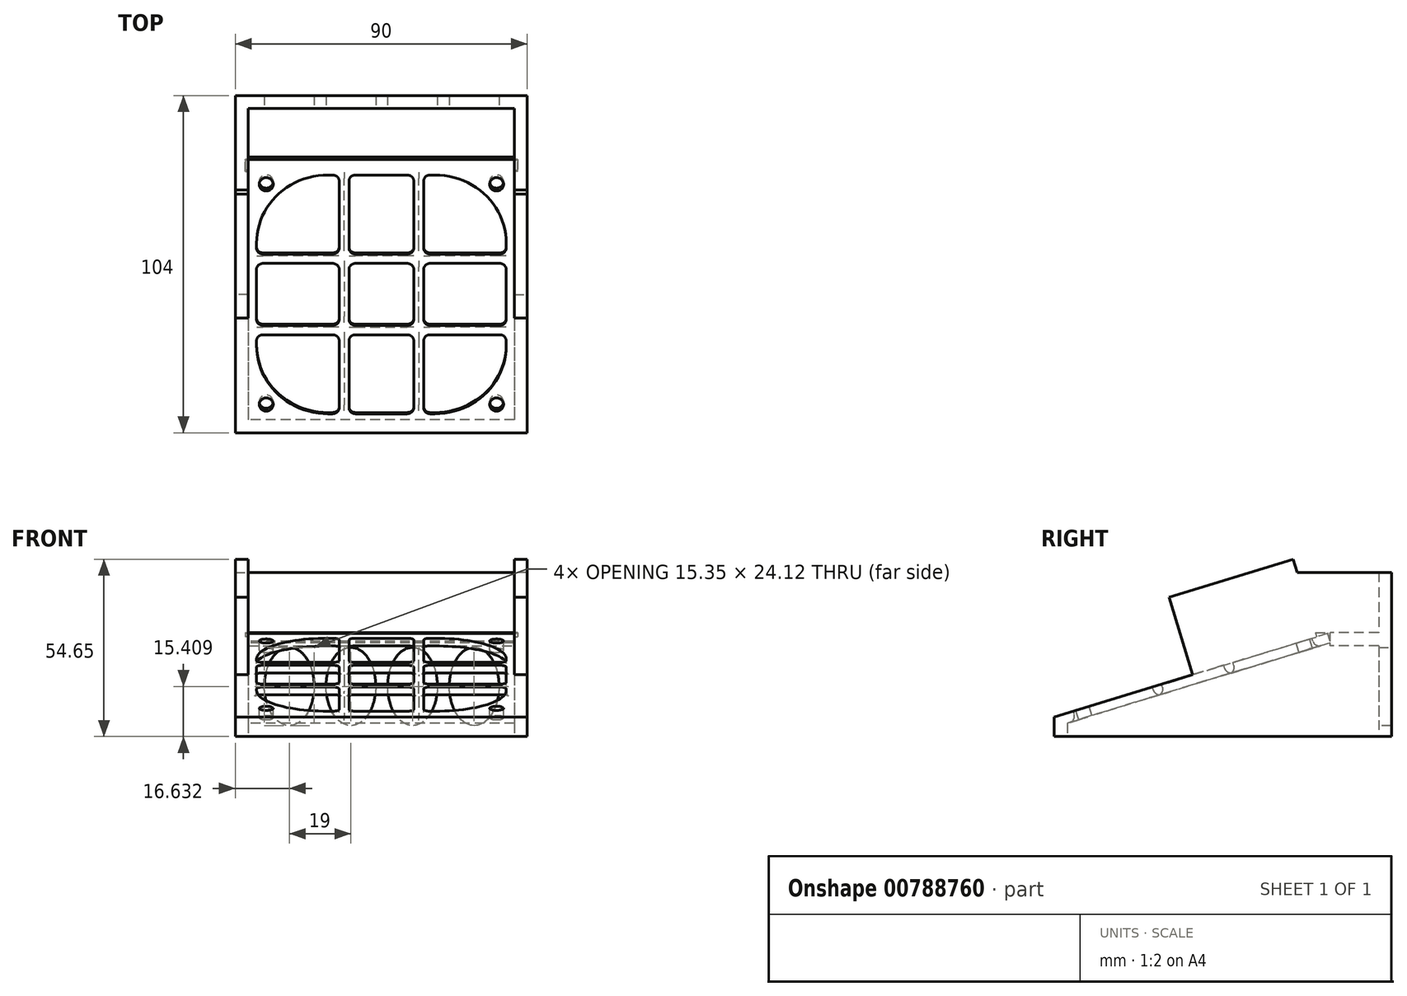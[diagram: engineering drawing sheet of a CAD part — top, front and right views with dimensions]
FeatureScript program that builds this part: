
annotation { "Feature Type Name" : "Feature", "Feature Type Description" : "" }
export const myFeature = defineFeature(function(context is Context, id is Id, definition is map)
    precondition{}
    {
        {
            var Q0;
            Q0=qCreatedBy(makeId("Top.planeOp"),FACE);
            var sketch = newSketch(context, id + "F0", { "sketchPlane" : qUnion([Q0])});
            skLineSegment(sketch, "E0.bottom", {"start": v(44.97, 44.9) * mm, "end": v(-45.03, 44.9) * mm, "construction": true});
            skLineSegment(sketch, "E0.top", {"start": v(44.97, -41.1) * mm, "end": v(-45.03, -41.1) * mm});
            skLineSegment(sketch, "E0.left", {"start": v(44.97, 44.9) * mm, "end": v(44.97, -41.1) * mm});
            skLineSegment(sketch, "E0.right", {"start": v(-45.03, 44.9) * mm, "end": v(-45.03, -41.1) * mm});
            skPoint(sketch, "E0.middle", {"position": v(0, 0) * mm});
            skLineSegment(sketch, "E1.0", {"start": v(40.97, 40.9) * mm, "end": v(-41.03, 40.9) * mm});
            skLineSegment(sketch, "E1.1", {"start": v(40.97, 40.9) * mm, "end": v(40.97, -37.1) * mm});
            skLineSegment(sketch, "E1.2", {"start": v(40.97, -37.1) * mm, "end": v(-41.03, -37.1) * mm});
            skLineSegment(sketch, "E1.3", {"start": v(-41.03, 40.9) * mm, "end": v(-41.03, -37.1) * mm});
            skLineSegment(sketch, "E2", {"start": v(-45.03, 44.9) * mm, "end": v(-45.03, 62.9) * mm});
            skLineSegment(sketch, "E3", {"start": v(-45.03, 62.9) * mm, "end": v(44.97, 62.9) * mm});
            skLineSegment(sketch, "E4", {"start": v(44.97, 62.9) * mm, "end": v(44.97, 44.9) * mm});
            skLineSegment(sketch, "E5", {"start": v(-41.03, 40.9) * mm, "end": v(-41.03, 58.9) * mm});
            skLineSegment(sketch, "E6", {"start": v(-41.03, 58.9) * mm, "end": v(40.97, 58.9) * mm});
            skLineSegment(sketch, "E7", {"start": v(40.97, 58.9) * mm, "end": v(40.97, 40.9) * mm});
            skSolve(sketch);
        }
        {
            var Q0;
            Q0=makeQuery(id+"F0.imprint","IMPRINT",FACE,{"disambiguationData":[TD([[makeQuery(id+"F0.imprint","IMPRINT",EDGE,{"derivedFrom":sQuery(id+"F0.wireOp",EDGE,"E0.top")}),-1.0]])]});
            var Q1;
            {var subQ0=sQuery(id+"F0.wireOp",EDGE,"E2");Q1=makeQuery(id+"F0.imprint","IMPRINT",FACE,{"disambiguationData":[TD([[makeQuery(id+"F0.imprint","IMPRINT",EDGE,{"derivedFrom":subQ0}),-1.0]])]});}
            extrude(context, id + "F1", {"entities" : qUnion([Q0, Q1]), "depth" : 32 * mm, "offsetDistance" : 25 * mm});
        }
        {
            var Q0;
            Q0=makeQuery(id+"F1.opExtrude","CAP_EDGE",EDGE,{"disambiguationData":[OSD([sQuery(id+"F0.wireOp",EDGE,"E0.top")])],"isStart":false});
            chamfer(context, id + "F2", {"entities" : qUnion([Q0]), "chamferType" : ChamferType.OFFSET_ANGLE, "width" : 26 * mm, "oppositeDirection" : false, "angle" : 73 * degree, "tangentPropagation" : true});
        }
        {
            var Q0;
            Q0=makeQuery(id+"F2.opChamfer","BLEND_FACE",FACE,{"disambiguationData":[OSD([sQuery(id+"F0.wireOp",EDGE,"E0.top")])]});
            var sketch = newSketch(context, id + "F3", { "sketchPlane" : qUnion([Q0])});
            skLineSegment(sketch, "E8.bottom", {"start": v(42, 50.58) * mm, "end": v(-42, 50.58) * mm});
            skLineSegment(sketch, "E8.top", {"start": v(42, -36.42) * mm, "end": v(-42, -36.42) * mm, "construction": true});
            skLineSegment(sketch, "E8.left", {"start": v(42, 50.58) * mm, "end": v(42, -36.42) * mm});
            skLineSegment(sketch, "E8.right", {"start": v(-42, 50.58) * mm, "end": v(-42, -36.42) * mm});
            skPoint(sketch, "E8.middle", {"position": v(0, 7.08) * mm});
            skLineSegment(sketch, "E9.bottom", {"start": v(16.5, 45.58) * mm, "end": v(13, 45.58) * mm});
            skLineSegment(sketch, "E9.top", {"start": v(16.5, -31.42) * mm, "end": v(13, -31.42) * mm});
            skLineSegment(sketch, "E9.left", {"start": v(38.5, 23.58) * mm, "end": v(38.5, 20.08) * mm});
            skLineSegment(sketch, "E9.right", {"start": v(-38.5, 23.58) * mm, "end": v(-38.5, 20.08) * mm});
            skArc(sketch, "E10.filletArc", {"start": v(38.5, 23.58) * mm, "mid": v(32.06, 39.14) * mm, "end": v(16.5, 45.58) * mm});
            skArc(sketch, "E11.filletArc", {"start": v(-16.5, 45.58) * mm, "mid": v(-32.06, 39.14) * mm, "end": v(-38.5, 23.58) * mm});
            skArc(sketch, "E12.filletArc", {"start": v(-38.5, -9.42) * mm, "mid": v(-32.06, -24.98) * mm, "end": v(-16.5, -31.42) * mm});
            skArc(sketch, "E13.filletArc", {"start": v(16.5, -31.42) * mm, "mid": v(32.06, -24.98) * mm, "end": v(38.5, -9.42) * mm});
            skLineSegment(sketch, "E14", {"start": v(16.5, -31.42) * mm, "end": v(16.5, 45.58) * mm, "construction": true});
            skLineSegment(sketch, "E15.bottom", {"start": v(35.5, 42.58) * mm, "end": v(-35.5, 42.58) * mm, "construction": true});
            skLineSegment(sketch, "E15.top", {"start": v(35.5, -28.42) * mm, "end": v(-35.5, -28.42) * mm, "construction": true});
            skLineSegment(sketch, "E15.left", {"start": v(35.5, 42.58) * mm, "end": v(35.5, -28.42) * mm, "construction": true});
            skLineSegment(sketch, "E15.right", {"start": v(-35.5, 42.58) * mm, "end": v(-35.5, -28.42) * mm, "construction": true});
            skCircle(sketch, "E16", {"center": v(-35.5, 42.58) * mm, "radius": 2.15 * mm});
            skCircle(sketch, "E17.MirrorC", {"center": v(35.5, 42.58) * mm, "radius": 2.15 * mm});
            skCircle(sketch, "E18.MirrorC", {"center": v(35.5, -28.42) * mm, "radius": 2.15 * mm});
            skCircle(sketch, "E19.MirrorC", {"center": v(-35.5, -28.42) * mm, "radius": 2.15 * mm});
            skLineSegment(sketch, "E20.bottom", {"start": v(40, 47.08) * mm, "end": v(-40, 47.08) * mm});
            skLineSegment(sketch, "E20.top", {"start": v(40, -32.92) * mm, "end": v(-40, -32.92) * mm});
            skLineSegment(sketch, "E20.left", {"start": v(40, 47.08) * mm, "end": v(40, -32.92) * mm});
            skLineSegment(sketch, "E20.right", {"start": v(-40, 47.08) * mm, "end": v(-40, -32.92) * mm});
            skLineSegment(sketch, "E21", {"start": v(-42, 7.08) * mm, "end": v(42, 7.08) * mm, "construction": true});
            skLineSegment(sketch, "E22", {"start": v(0, 50.58) * mm, "end": v(0, -36.42) * mm, "construction": true});
            skLineSegment(sketch, "E23", {"start": v(13, -31.42) * mm, "end": v(13, -5.92) * mm});
            skLineSegment(sketch, "E24", {"start": v(10, -31.42) * mm, "end": v(10, -5.92) * mm});
            skLineSegment(sketch, "E25.MirrorCS", {"start": v(-10, -31.42) * mm, "end": v(-10, -5.92) * mm});
            skLineSegment(sketch, "E26.MirrorCS", {"start": v(-13, -31.42) * mm, "end": v(-13, -5.92) * mm});
            skLineSegment(sketch, "E27.trimOffspring", {"start": v(-13, -31.42) * mm, "end": v(-16.5, -31.42) * mm});
            skLineSegment(sketch, "E28.trimOffspring", {"start": v(-13, 45.58) * mm, "end": v(-16.5, 45.58) * mm});
            skLineSegment(sketch, "E29.trimOffspring", {"start": v(10, 45.58) * mm, "end": v(-10, 45.58) * mm});
            skLineSegment(sketch, "E30.trimOffspring", {"start": v(10, -31.42) * mm, "end": v(-10, -31.42) * mm});
            skLineSegment(sketch, "E31", {"start": v(-38.5, -5.92) * mm, "end": v(-13, -5.92) * mm});
            skLineSegment(sketch, "E32", {"start": v(38.5, -2.92) * mm, "end": v(13, -2.92) * mm});
            skLineSegment(sketch, "E33", {"start": v(10, 45.58) * mm, "end": v(13, 45.58) * mm, "construction": true});
            skLineSegment(sketch, "E34.trimOffspring", {"start": v(38.5, -5.92) * mm, "end": v(38.5, -9.42) * mm});
            skLineSegment(sketch, "E35", {"start": v(38.5, -5.92) * mm, "end": v(38.5, -2.92) * mm, "construction": true});
            skPoint(sketch, "E36", {"position": v(35.5, 7.08) * mm});
            skPoint(sketch, "E37", {"position": v(0, 45.58) * mm});
            skLineSegment(sketch, "E38.MirrorCS", {"start": v(38.5, 17.08) * mm, "end": v(13, 17.08) * mm});
            skLineSegment(sketch, "E39.MirrorCS", {"start": v(-38.5, 20.08) * mm, "end": v(-13, 20.08) * mm});
            skLineSegment(sketch, "E40.trimOffspring", {"start": v(38.5, 17.08) * mm, "end": v(38.5, -2.92) * mm});
            skLineSegment(sketch, "E41.trimOffspring", {"start": v(-38.5, 17.08) * mm, "end": v(-38.5, -2.92) * mm});
            skLineSegment(sketch, "E42.trimOffspring", {"start": v(-38.5, -5.92) * mm, "end": v(-38.5, -9.42) * mm});
            skLineSegment(sketch, "E43.trimOffspring", {"start": v(-10, -2.92) * mm, "end": v(-10, 17.08) * mm});
            skLineSegment(sketch, "E44.trimOffspring", {"start": v(-13, -2.92) * mm, "end": v(-38.5, -2.92) * mm});
            skLineSegment(sketch, "E45.trimOffspring", {"start": v(-13, -2.92) * mm, "end": v(-13, 17.08) * mm});
            skLineSegment(sketch, "E46.trimOffspring", {"start": v(-10, -5.92) * mm, "end": v(10, -5.92) * mm});
            skLineSegment(sketch, "E47.trimOffspring", {"start": v(-13, 17.08) * mm, "end": v(-38.5, 17.08) * mm});
            skLineSegment(sketch, "E48.trimOffspring", {"start": v(-13, 20.08) * mm, "end": v(-13, 45.58) * mm});
            skLineSegment(sketch, "E49.trimOffspring", {"start": v(-10, 20.08) * mm, "end": v(10, 20.08) * mm});
            skLineSegment(sketch, "E50.trimOffspring", {"start": v(-10, 20.08) * mm, "end": v(-10, 45.58) * mm});
            skLineSegment(sketch, "E51.trimOffspring", {"start": v(13, 20.08) * mm, "end": v(13, 45.58) * mm});
            skLineSegment(sketch, "E52.trimOffspring", {"start": v(10, 17.08) * mm, "end": v(-10, 17.08) * mm});
            skLineSegment(sketch, "E53.trimOffspring", {"start": v(10, 20.08) * mm, "end": v(10, 45.58) * mm});
            skLineSegment(sketch, "E54.trimOffspring", {"start": v(13, 20.08) * mm, "end": v(38.5, 20.08) * mm});
            skLineSegment(sketch, "E55.trimOffspring", {"start": v(13, -2.92) * mm, "end": v(13, 17.08) * mm});
            skLineSegment(sketch, "E56.trimOffspring", {"start": v(10, -2.92) * mm, "end": v(-10, -2.92) * mm});
            skLineSegment(sketch, "E57.trimOffspring", {"start": v(10, -2.92) * mm, "end": v(10, 17.08) * mm});
            skLineSegment(sketch, "E58.trimOffspring", {"start": v(13, -5.92) * mm, "end": v(38.5, -5.92) * mm});
            skLineSegment(sketch, "E59", {"start": v(-40, -32.92) * mm, "end": v(-42, -32.92) * mm});
            skLineSegment(sketch, "E60", {"start": v(40, -32.92) * mm, "end": v(42, -32.92) * mm});
            skLineSegment(sketch, "E61", {"start": v(-42, -34.56) * mm, "end": v(42, -34.56) * mm});
            skLineSegment(sketch, "E62", {"start": v(-42, -36.42) * mm, "end": v(-42, -37.56) * mm, "construction": true});
            skLineSegment(sketch, "E63", {"start": v(-42, -37.56) * mm, "end": v(42, -37.56) * mm});
            skLineSegment(sketch, "E64", {"start": v(42, -37.56) * mm, "end": v(42, -36.42) * mm, "construction": true});
            skLineSegment(sketch, "E65", {"start": v(-42, -34.56) * mm, "end": v(-45.03, -34.56) * mm});
            skLineSegment(sketch, "E66", {"start": v(-45.03, -34.56) * mm, "end": v(-45.03, -37.56) * mm});
            skLineSegment(sketch, "E67", {"start": v(-45.03, -37.56) * mm, "end": v(-42, -37.56) * mm});
            skLineSegment(sketch, "E68", {"start": v(42, -34.56) * mm, "end": v(44.97, -34.56) * mm});
            skLineSegment(sketch, "E69", {"start": v(44.97, -34.56) * mm, "end": v(44.97, -37.56) * mm});
            skLineSegment(sketch, "E70", {"start": v(44.97, -37.56) * mm, "end": v(42, -37.56) * mm});
            skLineSegment(sketch, "E71", {"start": v(40, 47.08) * mm, "end": v(42, 47.08) * mm});
            skLineSegment(sketch, "E72", {"start": v(-40, 47.08) * mm, "end": v(-42, 47.08) * mm});
            skLineSegment(sketch, "E73", {"start": v(40.97, 47.08) * mm, "end": v(44.97, 47.08) * mm});
            skLineSegment(sketch, "E74", {"start": v(-41.03, 47.08) * mm, "end": v(-45.03, 47.08) * mm});
            skLineSegment(sketch, "E75", {"start": v(-41.03, 7.08) * mm, "end": v(-45.03, 7.08) * mm});
            skLineSegment(sketch, "E76", {"start": v(40.97, 7.08) * mm, "end": v(44.97, 7.08) * mm});
            skSolve(sketch);
        }
        {
            var Q0;
            Q0 = qSketchRegion(id + "F3", true);
            var Q1;
            {var subQ42=sQuery(id+"F3.wireOp",EDGE,"E9.top");Q1=makeQuery(id+"F3.imprint","IMPRINT",FACE,{"disambiguationData":[TD([[makeQuery(id+"F3.imprint","IMPRINT",EDGE,{"derivedFrom":subQ42}),1.0]])]});}
            var Q2;
            {var subQ0=sQuery(id+"F3.wireOp",EDGE,"E13.filletArc");var subQ1=makeQuery(id+"F1.opExtrude","CAP_EDGE",EDGE,{"disambiguationData":[OSD([sQuery(id+"F0.wireOp",EDGE,"E0.top")])],"isStart":false});var subQ2=makeQuery(id+"F2.opChamfer","BLEND_EDGE",EDGE,{"blendedFrom":[subQ1,makeQuery(id+"F1.opExtrude","SWEPT_FACE",FACE,{"disambiguationData":[OSD([sQuery(id+"F0.wireOp",EDGE,"E1.2")])]})],"blendedInto":[makeQuery(id+"F1.opExtrude","SWEPT_FACE",FACE,{"disambiguationData":[OSD([sQuery(id+"F0.wireOp",EDGE,"E1.2")])]})]});var subQ3=makeQuery(id+"F3.imprint","INTERSECT",VERTEX,{"derivedFrom":[subQ2,subQ0]});Q2=makeQuery(id+"F3.imprint","IMPRINT",FACE,{"disambiguationData":[TD([[makeQuery(id+"F3.imprint","IMPRINT",EDGE,{"disambiguationData":[TD([[subQ3,-1.0]])],"derivedFrom":subQ0}),-1.0]])]});}
            var Q3;
            {var subQ0=sQuery(id+"F3.wireOp",EDGE,"E12.filletArc");var subQ1=makeQuery(id+"F1.opExtrude","CAP_EDGE",EDGE,{"disambiguationData":[OSD([sQuery(id+"F0.wireOp",EDGE,"E0.top")])],"isStart":false});var subQ2=makeQuery(id+"F2.opChamfer","BLEND_EDGE",EDGE,{"blendedFrom":[subQ1,makeQuery(id+"F1.opExtrude","SWEPT_FACE",FACE,{"disambiguationData":[OSD([sQuery(id+"F0.wireOp",EDGE,"E1.3")])]})],"blendedInto":[makeQuery(id+"F1.opExtrude","SWEPT_FACE",FACE,{"disambiguationData":[OSD([sQuery(id+"F0.wireOp",EDGE,"E1.3")])]})]});var subQ3=makeQuery(id+"F3.imprint","INTERSECT",VERTEX,{"derivedFrom":[subQ2,subQ0]});Q3=makeQuery(id+"F3.imprint","IMPRINT",FACE,{"disambiguationData":[TD([[makeQuery(id+"F3.imprint","IMPRINT",EDGE,{"disambiguationData":[TD([[subQ3,-1.0]])],"derivedFrom":subQ0}),-1.0]])]});}
            var Q4;
            {var subQ11=sQuery(id+"F3.wireOp",EDGE,"E9.bottom");Q4=makeQuery(id+"F3.imprint","IMPRINT",FACE,{"disambiguationData":[TD([[makeQuery(id+"F3.imprint","IMPRINT",EDGE,{"derivedFrom":subQ11}),-1.0]])]});}
            extrude(context, id + "F4", {"entities" : qUnion([Q0, Q1, Q2, Q3, Q4]), "operationType" : NewBodyOperationType.ADD, "oppositeDirection" : true, "depth" : 3 * mm, "offsetDistance" : 25 * mm});
        }
        {
            var Q0;
            Q0=makeQuery(id+"F1.opExtrude","SWEPT_FACE",FACE,{"disambiguationData":[OSD([sQuery(id+"F0.wireOp",EDGE,"E3")])]});
            var sketch = newSketch(context, id + "F5", { "sketchPlane" : qUnion([Q0])});
            skEllipse(sketch, "E77", {"center": v(-28.6, 15.4) * mm, "majorRadius": 12.06 * mm, "minorRadius": 7.68 * mm, "majorAxis": v(0, 1)});
            skEllipse(sketch, "E78.1.0.0", {"center": v(-9.6, 15.4) * mm, "majorRadius": 12.06 * mm, "minorRadius": 7.68 * mm, "majorAxis": v(0, 1)});
            skEllipse(sketch, "E78.2.0.0", {"center": v(9.4, 15.4) * mm, "majorRadius": 12.06 * mm, "minorRadius": 7.68 * mm, "majorAxis": v(0, 1)});
            skEllipse(sketch, "E78.3.0.0", {"center": v(28.4, 15.4) * mm, "majorRadius": 12.06 * mm, "minorRadius": 7.68 * mm, "majorAxis": v(0, 1)});
            skLineSegment(sketch, "E78.direction1", {"start": v(-28.6, 15.4) * mm, "end": v(-9.6, 15.4) * mm, "construction": true});
            skSolve(sketch);
        }
        {
            var Q0;
            Q0 = qSketchRegion(id + "F5", true);
            extrude(context, id + "F6", {"entities" : qUnion([Q0]), "operationType" : NewBodyOperationType.REMOVE, "oppositeDirection" : true, "depth" : 5 * mm, "offsetDistance" : 25 * mm});
        }
        {
            var Q0;
            Q0=makeQuery(id+"F4.opExtrude","SWEPT_EDGE",EDGE,{"disambiguationData":[OSD([sQuery(id+"F3.wireOp",EDGE,"E45.trimOffspring"),sQuery(id+"F3.wireOp",EDGE,"E47.trimOffspring")])]});
            var Q1;
            Q1=makeQuery(id+"F4.opExtrude","SWEPT_EDGE",EDGE,{"disambiguationData":[OSD([sQuery(id+"F3.wireOp",EDGE,"E52.trimOffspring"),sQuery(id+"F3.wireOp",EDGE,"E57.trimOffspring")])]});
            var Q2;
            Q2=makeQuery(id+"F4.opExtrude","SWEPT_EDGE",EDGE,{"disambiguationData":[OSD([sQuery(id+"F3.wireOp",EDGE,"E24"),sQuery(id+"F3.wireOp",EDGE,"E46.trimOffspring")])]});
            var Q3;
            Q3=makeQuery(id+"F4.opExtrude","SWEPT_EDGE",EDGE,{"disambiguationData":[OSD([sQuery(id+"F3.wireOp",EDGE,"E26.MirrorCS"),sQuery(id+"F3.wireOp",EDGE,"E31")])]});
            var Q4;
            Q4=makeQuery(id+"F4.opExtrude","SWEPT_EDGE",EDGE,{"disambiguationData":[OSD([sQuery(id+"F3.wireOp",EDGE,"E25.MirrorCS"),sQuery(id+"F3.wireOp",EDGE,"E46.trimOffspring")])]});
            var Q5;
            Q5=makeQuery(id+"F4.opExtrude","SWEPT_EDGE",EDGE,{"disambiguationData":[OSD([sQuery(id+"F3.wireOp",EDGE,"E43.trimOffspring"),sQuery(id+"F3.wireOp",EDGE,"E52.trimOffspring")])]});
            var Q6;
            Q6=makeQuery(id+"F4.opExtrude","SWEPT_EDGE",EDGE,{"disambiguationData":[OSD([sQuery(id+"F3.wireOp",EDGE,"E41.trimOffspring"),sQuery(id+"F3.wireOp",EDGE,"E47.trimOffspring")])]});
            var Q7;
            Q7=makeQuery(id+"F4.opExtrude","SWEPT_EDGE",EDGE,{"disambiguationData":[OSD([sQuery(id+"F3.wireOp",EDGE,"E31"),sQuery(id+"F3.wireOp",EDGE,"E42.trimOffspring")])]});
            var Q8;
            Q8=makeQuery(id+"F4.opExtrude","SWEPT_EDGE",EDGE,{"disambiguationData":[OSD([sQuery(id+"F3.wireOp",EDGE,"E23"),sQuery(id+"F3.wireOp",EDGE,"E58.trimOffspring")])]});
            var Q9;
            Q9=makeQuery(id+"F4.opExtrude","SWEPT_EDGE",EDGE,{"disambiguationData":[OSD([sQuery(id+"F3.wireOp",EDGE,"E38.MirrorCS"),sQuery(id+"F3.wireOp",EDGE,"E55.trimOffspring")])]});
            var Q10;
            Q10=makeQuery(id+"F4.opExtrude","SWEPT_EDGE",EDGE,{"disambiguationData":[OSD([sQuery(id+"F3.wireOp",EDGE,"E9.bottom"),sQuery(id+"F3.wireOp",EDGE,"E51.trimOffspring")])]});
            var Q11;
            Q11=makeQuery(id+"F4.opExtrude","SWEPT_EDGE",EDGE,{"disambiguationData":[OSD([sQuery(id+"F3.wireOp",EDGE,"E29.trimOffspring"),sQuery(id+"F3.wireOp",EDGE,"E50.trimOffspring")])]});
            var Q12;
            Q12=makeQuery(id+"F4.opExtrude","SWEPT_EDGE",EDGE,{"disambiguationData":[OSD([sQuery(id+"F3.wireOp",EDGE,"E38.MirrorCS"),sQuery(id+"F3.wireOp",EDGE,"E40.trimOffspring")])]});
            var Q13;
            Q13=makeQuery(id+"F4.opExtrude","SWEPT_EDGE",EDGE,{"disambiguationData":[OSD([sQuery(id+"F3.wireOp",EDGE,"E34.trimOffspring"),sQuery(id+"F3.wireOp",EDGE,"E58.trimOffspring")])]});
            var Q14;
            Q14=makeQuery(id+"F4.opExtrude","SWEPT_EDGE",EDGE,{"disambiguationData":[OSD([sQuery(id+"F3.wireOp",EDGE,"E29.trimOffspring"),sQuery(id+"F3.wireOp",EDGE,"E53.trimOffspring")])]});
            var Q15;
            Q15=makeQuery(id+"F4.opExtrude","SWEPT_EDGE",EDGE,{"disambiguationData":[OSD([sQuery(id+"F3.wireOp",EDGE,"E28.trimOffspring"),sQuery(id+"F3.wireOp",EDGE,"E48.trimOffspring")])]});
            var Q16;
            Q16=makeQuery(id+"F4.opExtrude","SWEPT_EDGE",EDGE,{"disambiguationData":[OSD([sQuery(id+"F3.wireOp",EDGE,"E25.MirrorCS"),sQuery(id+"F3.wireOp",EDGE,"E30.trimOffspring")])]});
            var Q17;
            Q17=makeQuery(id+"F4.opExtrude","SWEPT_EDGE",EDGE,{"disambiguationData":[OSD([sQuery(id+"F3.wireOp",EDGE,"E9.top"),sQuery(id+"F3.wireOp",EDGE,"E23")])]});
            var Q18;
            Q18=makeQuery(id+"F4.opExtrude","SWEPT_EDGE",EDGE,{"disambiguationData":[OSD([sQuery(id+"F3.wireOp",EDGE,"E32"),sQuery(id+"F3.wireOp",EDGE,"E55.trimOffspring")])]});
            var Q19;
            Q19=makeQuery(id+"F4.opExtrude","SWEPT_EDGE",EDGE,{"disambiguationData":[OSD([sQuery(id+"F3.wireOp",EDGE,"E51.trimOffspring"),sQuery(id+"F3.wireOp",EDGE,"E54.trimOffspring")])]});
            var Q20;
            Q20=makeQuery(id+"F4.opExtrude","SWEPT_EDGE",EDGE,{"disambiguationData":[OSD([sQuery(id+"F3.wireOp",EDGE,"E49.trimOffspring"),sQuery(id+"F3.wireOp",EDGE,"E50.trimOffspring")])]});
            var Q21;
            Q21=makeQuery(id+"F4.opExtrude","SWEPT_EDGE",EDGE,{"disambiguationData":[OSD([sQuery(id+"F3.wireOp",EDGE,"E43.trimOffspring"),sQuery(id+"F3.wireOp",EDGE,"E56.trimOffspring")])]});
            var Q22;
            Q22=makeQuery(id+"F4.opExtrude","SWEPT_EDGE",EDGE,{"disambiguationData":[OSD([sQuery(id+"F3.wireOp",EDGE,"E41.trimOffspring"),sQuery(id+"F3.wireOp",EDGE,"E44.trimOffspring")])]});
            var Q23;
            Q23=makeQuery(id+"F4.opExtrude","SWEPT_EDGE",EDGE,{"disambiguationData":[OSD([sQuery(id+"F3.wireOp",EDGE,"E9.right"),sQuery(id+"F3.wireOp",EDGE,"E39.MirrorCS")])]});
            var Q24;
            Q24=makeQuery(id+"F4.opExtrude","SWEPT_EDGE",EDGE,{"disambiguationData":[OSD([sQuery(id+"F3.wireOp",EDGE,"E39.MirrorCS"),sQuery(id+"F3.wireOp",EDGE,"E48.trimOffspring")])]});
            var Q25;
            Q25=makeQuery(id+"F4.opExtrude","SWEPT_EDGE",EDGE,{"disambiguationData":[OSD([sQuery(id+"F3.wireOp",EDGE,"E24"),sQuery(id+"F3.wireOp",EDGE,"E30.trimOffspring")])]});
            var Q26;
            Q26=makeQuery(id+"F4.opExtrude","SWEPT_EDGE",EDGE,{"disambiguationData":[OSD([sQuery(id+"F3.wireOp",EDGE,"E26.MirrorCS"),sQuery(id+"F3.wireOp",EDGE,"E27.trimOffspring")])]});
            var Q27;
            Q27=makeQuery(id+"F4.opExtrude","SWEPT_EDGE",EDGE,{"disambiguationData":[OSD([sQuery(id+"F3.wireOp",EDGE,"E32"),sQuery(id+"F3.wireOp",EDGE,"E40.trimOffspring")])]});
            var Q28;
            Q28=makeQuery(id+"F4.opExtrude","SWEPT_EDGE",EDGE,{"disambiguationData":[OSD([sQuery(id+"F3.wireOp",EDGE,"E9.left"),sQuery(id+"F3.wireOp",EDGE,"E54.trimOffspring")])]});
            var Q29;
            Q29=makeQuery(id+"F4.opExtrude","SWEPT_EDGE",EDGE,{"disambiguationData":[OSD([sQuery(id+"F3.wireOp",EDGE,"E56.trimOffspring"),sQuery(id+"F3.wireOp",EDGE,"E57.trimOffspring")])]});
            var Q30;
            Q30=makeQuery(id+"F4.opExtrude","SWEPT_EDGE",EDGE,{"disambiguationData":[OSD([sQuery(id+"F3.wireOp",EDGE,"E49.trimOffspring"),sQuery(id+"F3.wireOp",EDGE,"E53.trimOffspring")])]});
            var Q31;
            Q31=makeQuery(id+"F4.opExtrude","SWEPT_EDGE",EDGE,{"disambiguationData":[OSD([sQuery(id+"F3.wireOp",EDGE,"E44.trimOffspring"),sQuery(id+"F3.wireOp",EDGE,"E45.trimOffspring")])]});
            fillet(context, id + "F7", {"entities" : qUnion([Q0, Q1, Q2, Q3, Q4, Q5, Q6, Q7, Q8, Q9, Q10, Q11, Q12, Q13, Q14, Q15, Q16, Q17, Q18, Q19, Q20, Q21, Q22, Q23, Q24, Q25, Q26, Q27, Q28, Q29, Q30, Q31]), "radius" : 2 * mm, "tangentPropagation" : true, "allowEdgeOverflow" : false});
        }
        {
            var Q0;
            Q0=makeQuery(id+"F4.opExtrude","CAP_EDGE",EDGE,{"disambiguationData":[OSD([sQuery(id+"F3.wireOp",EDGE,"E57.trimOffspring")])],"isStart":false});
            var Q1;
            Q1=makeQuery(id+"F4.opExtrude","CAP_EDGE",EDGE,{"disambiguationData":[OSD([sQuery(id+"F3.wireOp",EDGE,"E58.trimOffspring")])],"isStart":false});
            var Q2;
            Q2=makeQuery(id+"F4.opExtrude","CAP_EDGE",EDGE,{"disambiguationData":[OSD([sQuery(id+"F3.wireOp",EDGE,"E32")])],"isStart":false});
            var Q3;
            Q3=makeQuery(id+"F4.opExtrude","CAP_EDGE",EDGE,{"disambiguationData":[OSD([sQuery(id+"F3.wireOp",EDGE,"E25.MirrorCS")])],"isStart":false});
            var Q4;
            Q4=makeQuery(id+"F4.opExtrude","CAP_EDGE",EDGE,{"disambiguationData":[OSD([sQuery(id+"F3.wireOp",EDGE,"E26.MirrorCS")])],"isStart":false});
            var Q5;
            Q5=makeQuery(id+"F4.opExtrude","CAP_EDGE",EDGE,{"disambiguationData":[OSD([sQuery(id+"F3.wireOp",EDGE,"E44.trimOffspring")])],"isStart":false});
            var Q6;
            Q6=makeQuery(id+"F4.opExtrude","CAP_EDGE",EDGE,{"disambiguationData":[OSD([sQuery(id+"F3.wireOp",EDGE,"E39.MirrorCS")])],"isStart":false});
            var Q7;
            Q7=makeQuery(id+"F4.opExtrude","CAP_EDGE",EDGE,{"disambiguationData":[OSD([sQuery(id+"F3.wireOp",EDGE,"E49.trimOffspring")])],"isStart":false});
            var Q8;
            Q8=makeQuery(id+"F4.opExtrude","CAP_EDGE",EDGE,{"disambiguationData":[OSD([sQuery(id+"F3.wireOp",EDGE,"E54.trimOffspring")])],"isStart":false});
            var Q9;
            Q9=makeQuery(id+"F6.boolean.opBoolean","INTERSECT",EDGE,{"derivedFrom":[makeQuery(id+"F1.opExtrude","SWEPT_FACE",FACE,{"disambiguationData":[OSD([sQuery(id+"F0.wireOp",EDGE,"E1.0")])]}),makeQuery(id+"F6.opExtrude","SWEPT_FACE",FACE,{"disambiguationData":[OSD([sQuery(id+"F5.wireOp",EDGE,"0c994f2f-d3ee-4637-8eba-8318ff52502f.2")])]})]});
            fillet(context, id + "F8", {"entities" : qUnion([Q0, Q1, Q2, Q3, Q4, Q5, Q6, Q7, Q8, Q9]), "radius" : 2 * mm, "tangentPropagation" : true, "allowEdgeOverflow" : false});
        }
        {
            var Q0;
            Q0=makeQuery(id+"F1.opExtrude","CAP_FACE",FACE,{"disambiguationData":[OSD([sQuery(id+"F0.wireOp",EDGE,"E0.top"),sQuery(id+"F0.wireOp",EDGE,"E0.left"),sQuery(id+"F0.wireOp",EDGE,"E0.right"),sQuery(id+"F0.wireOp",EDGE,"E1.1"),sQuery(id+"F0.wireOp",EDGE,"E1.2"),sQuery(id+"F0.wireOp",EDGE,"E1.3"),sQuery(id+"F0.wireOp",EDGE,"E2"),sQuery(id+"F0.wireOp",EDGE,"E3"),sQuery(id+"F0.wireOp",EDGE,"E4"),sQuery(id+"F0.wireOp",EDGE,"E5"),sQuery(id+"F0.wireOp",EDGE,"E6"),sQuery(id+"F0.wireOp",EDGE,"E7")])],"isStart":false});
            var sketch = newSketch(context, id + "F9", { "sketchPlane" : qUnion([Q0])});
            skLineSegment(sketch, "E79", {"start": v(40.97, 43.93) * mm, "end": v(-41.03, 43.93) * mm});
            skSolve(sketch);
        }
        {
            var Q0;
            Q0=makeQuery(id+"F9.imprint","IMPRINT",FACE,{"disambiguationData":[TD([[makeQuery(id+"F9.imprint","IMPRINT",EDGE,{"derivedFrom":sQuery(id+"F9.wireOp",EDGE,"E79")}),-1.0]])]});
            var Q1;
            {var subQ5=sQuery(id+"F0.wireOp",EDGE,"E3");Q1=makeQuery(id+"F9.imprint","IMPRINT",FACE,{"disambiguationData":[TD([[makeQuery(id+"F9.imprint","IMPRINT",EDGE,{"derivedFrom":makeQuery(id+"F1.opExtrude","CAP_EDGE",EDGE,{"disambiguationData":[OSD([subQ5])],"isStart":false})}),-1.0]])]});}
            extrude(context, id + "F10", {"entities" : qUnion([Q0, Q1]), "operationType" : NewBodyOperationType.ADD, "oppositeDirection" : true, "depth" : 4 * mm, "offsetDistance" : 25 * mm});
        }
        {
            var Q0;
            {var subQ5=sQuery(id+"F0.wireOp",EDGE,"E3");Q0=makeQuery(id+"F9.imprint","IMPRINT",FACE,{"disambiguationData":[TD([[makeQuery(id+"F9.imprint","IMPRINT",EDGE,{"derivedFrom":makeQuery(id+"F1.opExtrude","CAP_EDGE",EDGE,{"disambiguationData":[OSD([subQ5])],"isStart":false})}),-1.0]])]});}
            extrude(context, id + "F11", {"entities" : qUnion([Q0]), "depth" : 18.6 * mm, "offsetDistance" : 25 * mm});
        }
        {
            var Q0;
            {var subQ0=sQuery(id+"F0.wireOp",EDGE,"E7");var subQ1=sQuery(id+"F0.wireOp",EDGE,"E6");var subQ2=sQuery(id+"F0.wireOp",EDGE,"E5");var subQ3=sQuery(id+"F0.wireOp",EDGE,"E4");var subQ4=sQuery(id+"F0.wireOp",EDGE,"E3");var subQ5=sQuery(id+"F0.wireOp",EDGE,"E2");var subQ6=sQuery(id+"F0.wireOp",EDGE,"E1.3");var subQ7=sQuery(id+"F0.wireOp",EDGE,"E1.2");var subQ8=sQuery(id+"F0.wireOp",EDGE,"E1.1");var subQ9=sQuery(id+"F0.wireOp",EDGE,"E0.right");var subQ10=sQuery(id+"F0.wireOp",EDGE,"E0.left");var subQ11=sQuery(id+"F0.wireOp",EDGE,"E0.top");Q0=makeQuery(id+"F11.opExtrude","SWEPT_FACE",FACE,{"disambiguationData":[OSD([subQ11,subQ10,subQ9,subQ8,subQ7,subQ6,subQ5,subQ4,subQ3,subQ2,subQ1,subQ0]),TDD([makeQuery(id+"F9.imprint","IMPRINT",EDGE,{"derivedFrom":makeQuery(id+"F2.opChamfer","BLEND_EDGE",EDGE,{"disambiguationData":[OD(1.0)],"blendedFrom":[makeQuery(id+"F1.opExtrude","CAP_EDGE",EDGE,{"disambiguationData":[OSD([subQ11])],"isStart":false}),makeQuery(id+"F1.opExtrude","CAP_FACE",FACE,{"disambiguationData":[OSD([subQ11,subQ10,subQ9,subQ8,subQ7,subQ6,subQ5,subQ4,subQ3,subQ2,subQ1,subQ0])],"isStart":false})],"blendedInto":[makeQuery(id+"F1.opExtrude","CAP_FACE",FACE,{"disambiguationData":[OSD([subQ11,subQ10,subQ9,subQ8,subQ7,subQ6,subQ5,subQ4,subQ3,subQ2,subQ1,subQ0])],"isStart":false})]})})])]});}
            var Q1;
            {var subQ0=sQuery(id+"F0.wireOp",EDGE,"E7");var subQ1=sQuery(id+"F0.wireOp",EDGE,"E6");var subQ2=sQuery(id+"F0.wireOp",EDGE,"E5");var subQ3=sQuery(id+"F0.wireOp",EDGE,"E4");var subQ4=sQuery(id+"F0.wireOp",EDGE,"E3");var subQ5=sQuery(id+"F0.wireOp",EDGE,"E2");var subQ6=sQuery(id+"F0.wireOp",EDGE,"E1.3");var subQ7=sQuery(id+"F0.wireOp",EDGE,"E1.2");var subQ8=sQuery(id+"F0.wireOp",EDGE,"E1.1");var subQ9=sQuery(id+"F0.wireOp",EDGE,"E0.right");var subQ10=sQuery(id+"F0.wireOp",EDGE,"E0.left");var subQ11=sQuery(id+"F0.wireOp",EDGE,"E0.top");Q1=makeQuery(id+"F11.opExtrude","SWEPT_FACE",FACE,{"disambiguationData":[OSD([subQ11,subQ10,subQ9,subQ8,subQ7,subQ6,subQ5,subQ4,subQ3,subQ2,subQ1,subQ0]),TDD([makeQuery(id+"F9.imprint","IMPRINT",EDGE,{"derivedFrom":makeQuery(id+"F2.opChamfer","BLEND_EDGE",EDGE,{"disambiguationData":[OD(0.0)],"blendedFrom":[makeQuery(id+"F1.opExtrude","CAP_EDGE",EDGE,{"disambiguationData":[OSD([subQ11])],"isStart":false}),makeQuery(id+"F1.opExtrude","CAP_FACE",FACE,{"disambiguationData":[OSD([subQ11,subQ10,subQ9,subQ8,subQ7,subQ6,subQ5,subQ4,subQ3,subQ2,subQ1,subQ0])],"isStart":false})],"blendedInto":[makeQuery(id+"F1.opExtrude","CAP_FACE",FACE,{"disambiguationData":[OSD([subQ11,subQ10,subQ9,subQ8,subQ7,subQ6,subQ5,subQ4,subQ3,subQ2,subQ1,subQ0])],"isStart":false})]})})])]});}
            extrude(context, id + "F12", {"entities" : qUnion([Q0, Q1]), "operationType" : NewBodyOperationType.ADD, "depth" : 11.3 * mm, "offsetDistance" : 25 * mm});
        }
        {
            var Q0;
            {var subQ0=sQuery(id+"F3.wireOp",EDGE,"E74");var subQ1=sQuery(id+"F3.wireOp",EDGE,"E8.right");var subQ2=makeQuery(id+"F3.imprint","INTERSECT",VERTEX,{"derivedFrom":[subQ1,subQ0]});Q0=makeQuery(id+"F3.imprint","IMPRINT",FACE,{"disambiguationData":[TD([[makeQuery(id+"F3.imprint","IMPRINT",EDGE,{"disambiguationData":[TD([[subQ2,-1.0]])],"derivedFrom":subQ1}),-1.0]])]});}
            var Q1;
            {var subQ0=sQuery(id+"F3.wireOp",EDGE,"E74");var subQ1=sQuery(id+"F3.wireOp",EDGE,"E8.right");var subQ2=makeQuery(id+"F3.imprint","INTERSECT",VERTEX,{"derivedFrom":[subQ1,subQ0]});Q1=makeQuery(id+"F3.imprint","IMPRINT",FACE,{"disambiguationData":[TD([[makeQuery(id+"F3.imprint","IMPRINT",EDGE,{"disambiguationData":[TD([[subQ2,-1.0]])],"derivedFrom":subQ1}),1.0]])]});}
            var Q2;
            {var subQ0=sQuery(id+"F3.wireOp",EDGE,"E73");var subQ1=sQuery(id+"F3.wireOp",EDGE,"E8.left");var subQ2=makeQuery(id+"F3.imprint","INTERSECT",VERTEX,{"derivedFrom":[subQ1,subQ0]});Q2=makeQuery(id+"F3.imprint","IMPRINT",FACE,{"disambiguationData":[TD([[makeQuery(id+"F3.imprint","IMPRINT",EDGE,{"disambiguationData":[TD([[subQ2,-1.0]])],"derivedFrom":subQ1}),-1.0]])]});}
            var Q3;
            {var subQ0=sQuery(id+"F3.wireOp",EDGE,"E73");var subQ1=sQuery(id+"F3.wireOp",EDGE,"E8.left");var subQ2=makeQuery(id+"F3.imprint","INTERSECT",VERTEX,{"derivedFrom":[subQ1,subQ0]});Q3=makeQuery(id+"F3.imprint","IMPRINT",FACE,{"disambiguationData":[TD([[makeQuery(id+"F3.imprint","IMPRINT",EDGE,{"disambiguationData":[TD([[subQ2,-1.0]])],"derivedFrom":subQ1}),1.0]])]});}
            extrude(context, id + "F13", {"entities" : qUnion([Q0, Q1, Q2, Q3]), "operationType" : NewBodyOperationType.ADD, "depth" : 25 * mm, "offsetDistance" : 25 * mm});
        }
        {
            var Q0;
            {var subQ10=sQuery(id+"F3.wireOp",EDGE,"E8.left");var subQ12=sQuery(id+"F3.wireOp",EDGE,"E8.bottom");var subQ13=makeQuery(id+"F3.imprint","INTERSECT",VERTEX,{"derivedFrom":[subQ12,subQ10]});Q0=makeQuery(id+"F3.imprint","IMPRINT",FACE,{"disambiguationData":[TD([[makeQuery(id+"F3.imprint","IMPRINT",EDGE,{"disambiguationData":[TD([[subQ13,-1.0]])],"derivedFrom":subQ10}),1.0]])]});}
            var Q1;
            {var subQ10=sQuery(id+"F3.wireOp",EDGE,"E8.right");var subQ12=sQuery(id+"F3.wireOp",EDGE,"E8.bottom");var subQ13=makeQuery(id+"F3.imprint","INTERSECT",VERTEX,{"derivedFrom":[subQ12,subQ10]});Q1=makeQuery(id+"F3.imprint","IMPRINT",FACE,{"disambiguationData":[TD([[makeQuery(id+"F3.imprint","IMPRINT",EDGE,{"disambiguationData":[TD([[subQ13,-1.0]])],"derivedFrom":subQ10}),-1.0]])]});}
            extrude(context, id + "F14", {"entities" : qUnion([Q0, Q1]), "operationType" : NewBodyOperationType.ADD, "depth" : 4 * mm, "offsetDistance" : 25 * mm});
        }
    });
